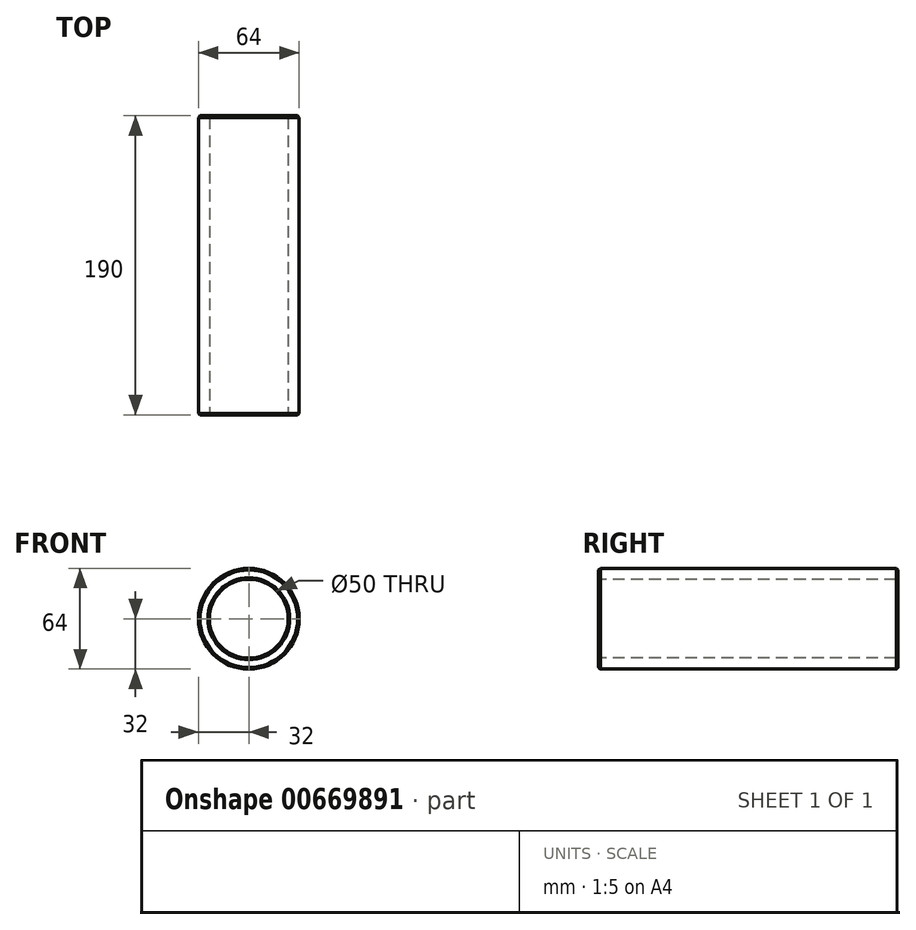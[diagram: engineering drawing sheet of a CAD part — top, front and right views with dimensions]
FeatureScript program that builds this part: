
annotation { "Feature Type Name" : "Feature", "Feature Type Description" : "" }
export const myFeature = defineFeature(function(context is Context, id is Id, definition is map)
    precondition{}
    {
        {
            var Q0;
            Q0=qCreatedBy(makeId("Top.planeOp"),FACE);
            var sketch = newSketch(context, id + "F0", { "sketchPlane" : qUnion([Q0])});
            skLineSegment(sketch, "E0.bottom", {"start": v(-25, 0) * mm, "end": v(-32, 0) * mm});
            skLineSegment(sketch, "E0.top", {"start": v(-25, 95) * mm, "end": v(-32, 95) * mm});
            skLineSegment(sketch, "E0.left", {"start": v(-25, 0) * mm, "end": v(-25, 95) * mm});
            skLineSegment(sketch, "E0.right", {"start": v(-32, 0) * mm, "end": v(-32, 95) * mm});
            skLineSegment(sketch, "E1.top", {"start": v(-25, -95) * mm, "end": v(-32, -95) * mm});
            skLineSegment(sketch, "E1.left", {"start": v(-25, 0) * mm, "end": v(-25, -95) * mm});
            skLineSegment(sketch, "E1.right", {"start": v(-32, 0) * mm, "end": v(-32, -95) * mm});
            skLineSegment(sketch, "E2", {"start": v(0, -95) * mm, "end": v(0, 95) * mm});
            skPoint(sketch, "E3.end.orphan", {"position": v(0, -100.51) * mm});
            skPoint(sketch, "E4.start.orphan", {"position": v(0, 0) * mm});
            skSolve(sketch);
        }
        {
            var Q0;
            Q0=makeQuery(id+"F0.imprint","IMPRINT",FACE,{"disambiguationData":[TD([[makeQuery(id+"F0.imprint","IMPRINT",EDGE,{"derivedFrom":sQuery(id+"F0.wireOp",EDGE,"E0.bottom")}),1.0]])]});
            var Q1;
            Q1=makeQuery(id+"F0.imprint","IMPRINT",FACE,{"disambiguationData":[TD([[makeQuery(id+"F0.imprint","IMPRINT",EDGE,{"derivedFrom":sQuery(id+"F0.wireOp",EDGE,"E0.top")}),1.0]])]});
            var Q2;
            Q2=sQuery(id+"F0.wireOp",EDGE,"E2");
            revolve(context, id + "F1", {"entities" : qUnion([Q0, Q1]), "axis" : qUnion([Q2]), "revolveType" : RevolveType.FULL});
        }
        {
            var Q0;
            Q0=makeQuery(id+"F1.opRevolve","SWEPT_FACE",FACE,{"disambiguationData":[OSD([sQuery(id+"F0.wireOp",EDGE,"E0.left"),sQuery(id+"F0.wireOp",EDGE,"E1.left")])]});
            chamfer(context, id + "F2", {"entities" : qUnion([Q0]), "width" : 1 * mm, "tangentPropagation" : true});
        }
        {
            var Q0;
            Q0=makeQuery(id+"F1.opRevolve","SWEPT_EDGE",EDGE,{"disambiguationData":[OSD([sQuery(id+"F0.wireOp",EDGE,"E1.top"),sQuery(id+"F0.wireOp",EDGE,"E1.right")])]});
            chamfer(context, id + "F3", {"entities" : qUnion([Q0]), "width" : 1 * mm, "tangentPropagation" : true});
        }
        {
            var Q0;
            Q0=makeQuery(id+"F1.opRevolve","SWEPT_EDGE",EDGE,{"disambiguationData":[OSD([sQuery(id+"F0.wireOp",EDGE,"E0.top"),sQuery(id+"F0.wireOp",EDGE,"E0.right")])]});
            chamfer(context, id + "F4", {"entities" : qUnion([Q0]), "width" : 1 * mm, "tangentPropagation" : true});
        }
    });
